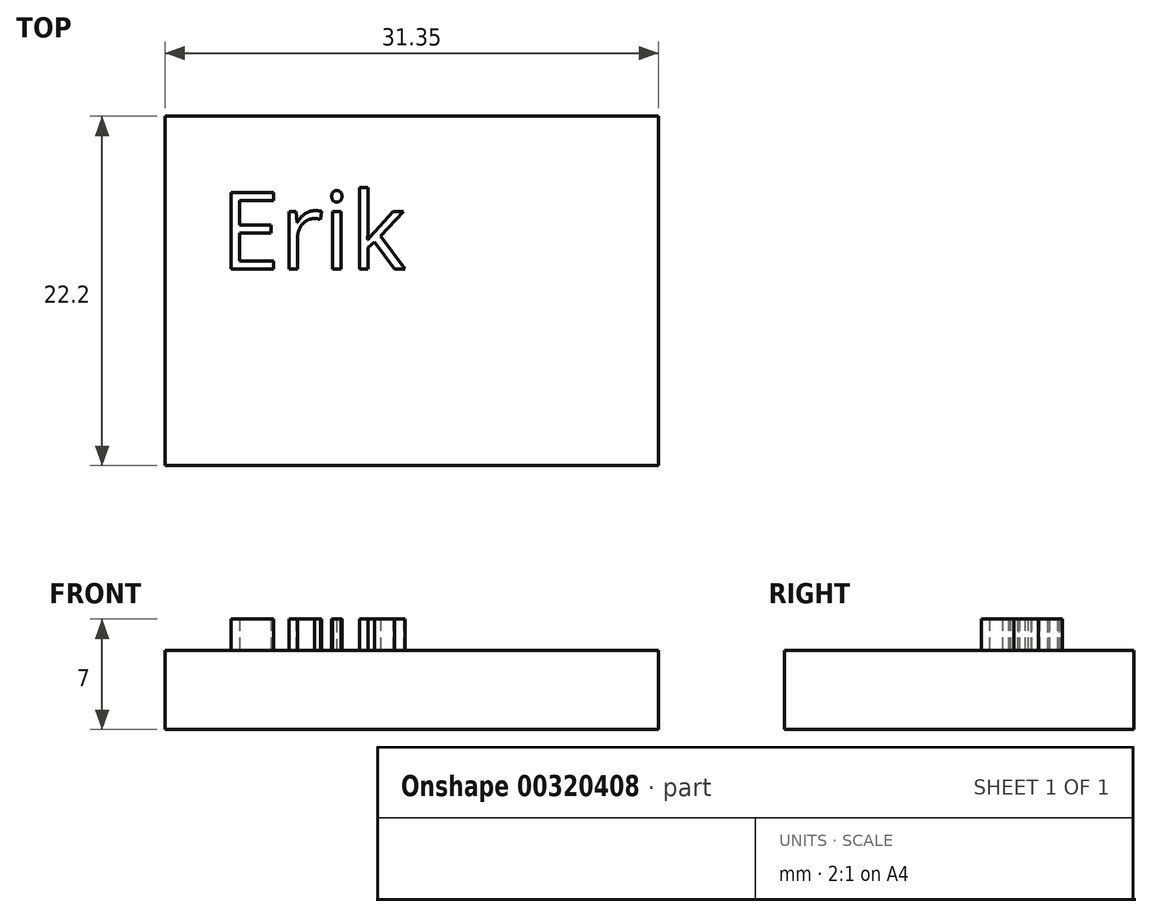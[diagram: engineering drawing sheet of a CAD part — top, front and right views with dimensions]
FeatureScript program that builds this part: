
annotation { "Feature Type Name" : "Feature", "Feature Type Description" : "" }
export const myFeature = defineFeature(function(context is Context, id is Id, definition is map)
    precondition{}
    {
        {
            var Q0;
            Q0=qCreatedBy(makeId("Top.planeOp"),FACE);
            var sketch = newSketch(context, id + "F0", { "sketchPlane" : qUnion([Q0])});
            skLineSegment(sketch, "E0.bottom", {"start": v(-17.54, 9.7) * mm, "end": v(13.8, 9.7) * mm});
            skLineSegment(sketch, "E0.top", {"start": v(-17.54, -12.5) * mm, "end": v(13.8, -12.5) * mm});
            skLineSegment(sketch, "E0.left", {"start": v(-17.54, 9.7) * mm, "end": v(-17.54, -12.5) * mm});
            skLineSegment(sketch, "E0.right", {"start": v(13.8, 9.7) * mm, "end": v(13.8, -12.5) * mm});
            skSolve(sketch);
        }
        {
            var Q0;
            Q0=makeQuery(id+"F0.imprint","IMPRINT",FACE,{"disambiguationData":[TD([[makeQuery(id+"F0.imprint","IMPRINT",EDGE,{"derivedFrom":sQuery(id+"F0.wireOp",EDGE,"E0.bottom")}),-1.0]])]});
            var Q1;
            Q1 = qSketchRegion(id + "F2", true);
            extrude(context, id + "F1", {"entities" : qUnion([Q0, Q1]), "depth" : 5 * mm});
        }
        {
            var Q0;
            Q0=makeQuery(id+"F1.opExtrude","CAP_FACE",FACE,{"disambiguationData":[OSD([sQuery(id+"F0.wireOp",EDGE,"E0.bottom"),sQuery(id+"F0.wireOp",EDGE,"E0.top"),sQuery(id+"F0.wireOp",EDGE,"E0.left"),sQuery(id+"F0.wireOp",EDGE,"E0.right")])],"isStart":false});
            var sketch = newSketch(context, id + "F2", { "sketchPlane" : qUnion([Q0])});
            skText(sketch, "E1", { "text": "Erik", "fontName": "OpenSans-Regular.ttf"});
            const initialGuessF2  = {"E1": [-0.01402, 0, 1, 0, 0.00488]};
            skSetInitialGuess(sketch, initialGuessF2);
            skSolve(sketch);
        }
        {
            var Q0;
            Q0 = qSketchRegion(id + "F2", true);
            extrude(context, id + "F3", {"entities" : qUnion([Q0]), "operationType" : NewBodyOperationType.ADD, "depth" : 2 * mm});
        }
    });
